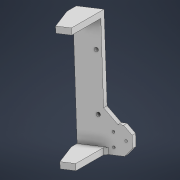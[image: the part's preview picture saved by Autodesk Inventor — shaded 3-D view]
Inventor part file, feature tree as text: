
AUTODESK INVENTOR PART (.ipt)
format: ipt  version: 2021 (Build 250183000, 183)  size: 313,344 bytes
history: native  units: mm
features: extrude x4, chamfer x4, sketch x4, other x1, mirror x1
ambient origin geometry x8: Origin, YZ Plane, XZ Plane, XY Plane, X Axis, Y Axis, Z Axis, Center Point
bodies: Solid1 (feature_tree)
feature tree (14):
  other  "psu holder left.ipt"
  extrude  "Extrusion1"  Depth=25.0mm
  extrude  "Extrusion2"  Depth=25.0mm
  mirror  "Mirror1"
  extrude  "Extrusion3"  TaperAngle=0.0deg  [1 undecoded]
  chamfer  "Chamfer1"  Distance=59.5mm
  chamfer  "Chamfer2"  [1 undecoded]
  chamfer  "Chamfer3"  Distance=25.0mm
  chamfer  "Chamfer4"  Distance=26.0mm
  extrude  "Extrusion4"  Depth=2.0mm
  sketch  "Sketch1"  dims[d0=10.0mm d1=25.0mm]
  sketch  "Sketch2"  dims[d2=25.0mm d3=25.0mm]
  sketch  "Sketch3"  dims[d4=6.0mm d5=0.0mm]
  sketch  "Sketch4"  dims[d10=6.0mm d11=59.5mm d12=0.0mm d13=25.0mm d14=26.0mm d15=13.0mm d16=12.0mm d17=15.0mm d18=2.5mm d19=30.0mm d21=360.0deg d23=6.0mm d24=0.0mm d25=7.5mm d26=2.0mm d27=45.0deg d28=12.5mm d29=2.0mm d30=45.0deg d31=3.0mm d32=2.0mm d33=45.0deg d34=40.0mm d35=40.0mm d36=15.0deg d37=5.0mm d38=4.0mm d39=4.0mm d40=54.0mm d41=26.5mm d42=26.5mm d43=0.0mm d44=0.0mm d9=0.5mm]
note: 2 required parameter values undecoded (feature->parameter linkage not recoverable at this tier; creation-order binding heuristic only, values carry confidence <= 0.55)
